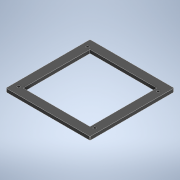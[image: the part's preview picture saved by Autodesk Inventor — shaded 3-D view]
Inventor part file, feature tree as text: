
AUTODESK INVENTOR PART (.ipt)
format: ipt  version: 2022 (Build 260153000, 153)  size: 136,704 bytes
history: native  units: mm
features: extrude x2, sketch x2, projected_geometry x1
ambient origin geometry x8: Origin, YZ Plane, XZ Plane, XY Plane, X Axis, Y Axis, Z Axis, Center Point
bodies: Solid1 (feature_tree)
feature tree (5):
  extrude  "Extrusion1"  Depth=10.0mm
  extrude  "Extrusion2"  Depth=4.0mm TaperAngle=0.0deg
  sketch  "Sketch1"  dims[d2=4.0mm d3=0.0mm d4=10.0mm]
  sketch  "Sketch2"  dims[d5=10.0mm d6=4.0mm d7=0.0mm]
  projected_geometry  "Projected Loop1"
